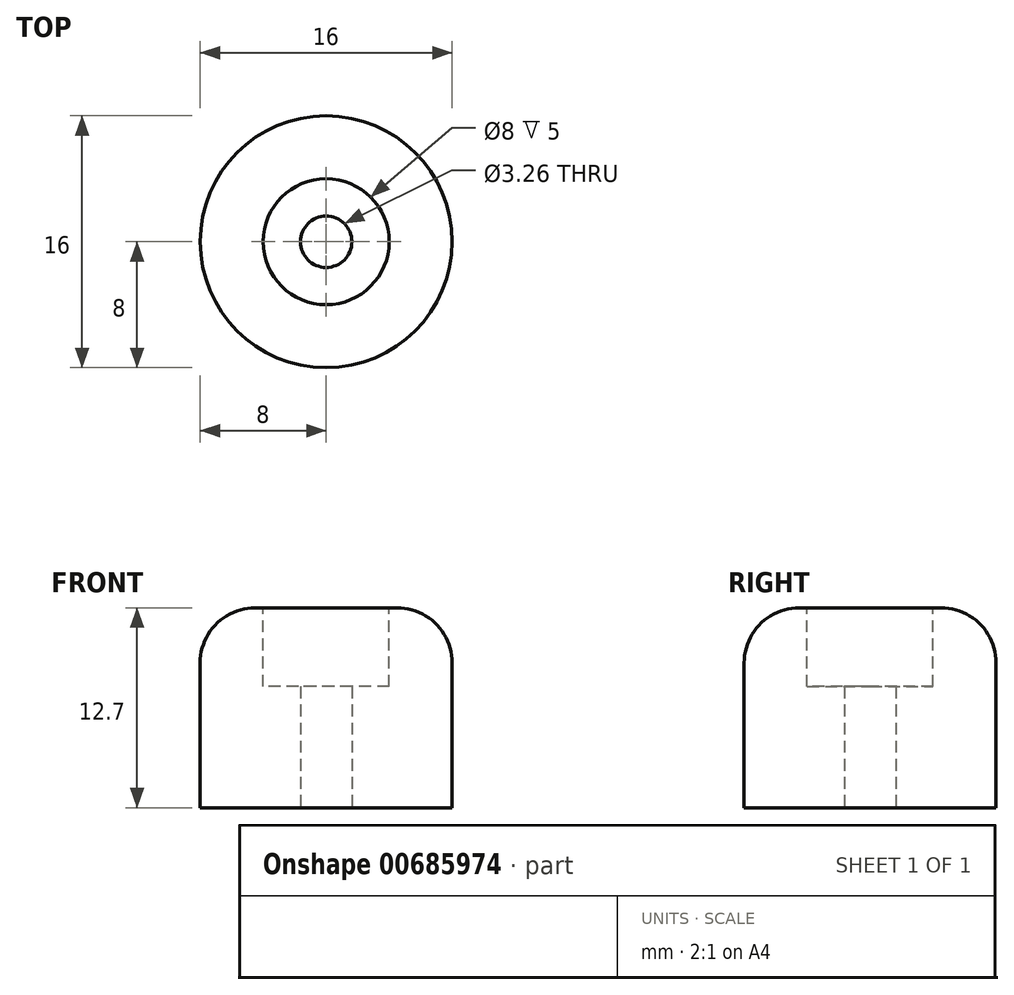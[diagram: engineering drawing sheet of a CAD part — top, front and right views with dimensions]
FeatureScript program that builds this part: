
annotation { "Feature Type Name" : "Feature", "Feature Type Description" : "" }
export const myFeature = defineFeature(function(context is Context, id is Id, definition is map)
    precondition{}
    {
        {
            var Q0;
            Q0=qCreatedBy(makeId("Top.planeOp"),FACE);
            var sketch = newSketch(context, id + "F0", { "sketchPlane" : qUnion([Q0])});
            skCircle(sketch, "E0", {"center": v(0, 0) * mm, "radius": 8 * mm});
            skSolve(sketch);
        }
        {
            var Q0;
            Q0=makeQuery(id+"F0.imprint","IMPRINT",FACE,{"disambiguationData":[TD([[makeQuery(id+"F0.imprint","IMPRINT",EDGE,{"derivedFrom":sQuery(id+"F0.wireOp",EDGE,"E0")}),1.0]])]});
            var Q1;
            Q1 = qSketchRegion(id + "F2", true);
            extrude(context, id + "F1", {"entities" : qUnion([Q0, Q1]), "depth" : 12.7 * mm, "offsetDistance" : 25 * mm});
        }
        {
            var Q0;
            Q0=makeQuery(id+"F1.opExtrude","CAP_FACE",FACE,{"disambiguationData":[OSD([sQuery(id+"F0.wireOp",EDGE,"E0")])],"isStart":false});
            var sketch = newSketch(context, id + "F2", { "sketchPlane" : qUnion([Q0])});
            skCircle(sketch, "E1", {"center": v(0, 0) * mm, "radius": 4 * mm});
            skSolve(sketch);
        }
        {
            var Q0;
            Q0=makeQuery(id+"F2.imprint","IMPRINT",FACE,{"disambiguationData":[TD([[makeQuery(id+"F2.imprint","IMPRINT",EDGE,{"derivedFrom":sQuery(id+"F2.wireOp",EDGE,"E1")}),1.0]])]});
            extrude(context, id + "F3", {"entities" : qUnion([Q0]), "operationType" : NewBodyOperationType.REMOVE, "oppositeDirection" : true, "depth" : 5 * mm, "offsetDistance" : 25 * mm});
        }
        {
            var Q0;
            Q0=sQuery(id+"F0.wireOp",VERTEX,"E0.center");
            var Q1;
            Q1=makeQuery(id+"F1.opExtrude","SWEPT_BODY",BODY,{"disambiguationData":[OSD([sQuery(id+"F0.wireOp",EDGE,"E0")])]});
            hole(context, id + "F4", {"style" : HoleStyle.SIMPLE, "endStyle" : HoleEndStyle.THROUGH, "oppositeDirection" : true, "standardTappedOrClearance" : lookupTablePath({ "fit" : "Normal (ASME)", "standard" : "ANSI", "size" : "#4", "type" : "Clearance" }), "standardBlindInLast" : lookupTablePath({ "fit" : "Free", "standard" : "ANSI", "size" : "#4", "type" : "Clearance" }), "holeDiameter" : 3.26 * mm, "majorDiameter" : 5 * mm, "isTappedThrough" : true, "tappedDepth" : 12 * mm, "tapClearance" : 3, "locations" : qUnion([Q0]), "scope" : qUnion([Q1])});
        }
        {
            var Q0;
            Q0=makeQuery(id+"F1.opExtrude","CAP_EDGE",EDGE,{"disambiguationData":[OSD([sQuery(id+"F0.wireOp",EDGE,"E0")])],"isStart":false});
            fillet(context, id + "F5", {"entities" : qUnion([Q0]), "radius" : 3.5 * mm, "tangentPropagation" : true, "allowEdgeOverflow" : false});
        }
    });
